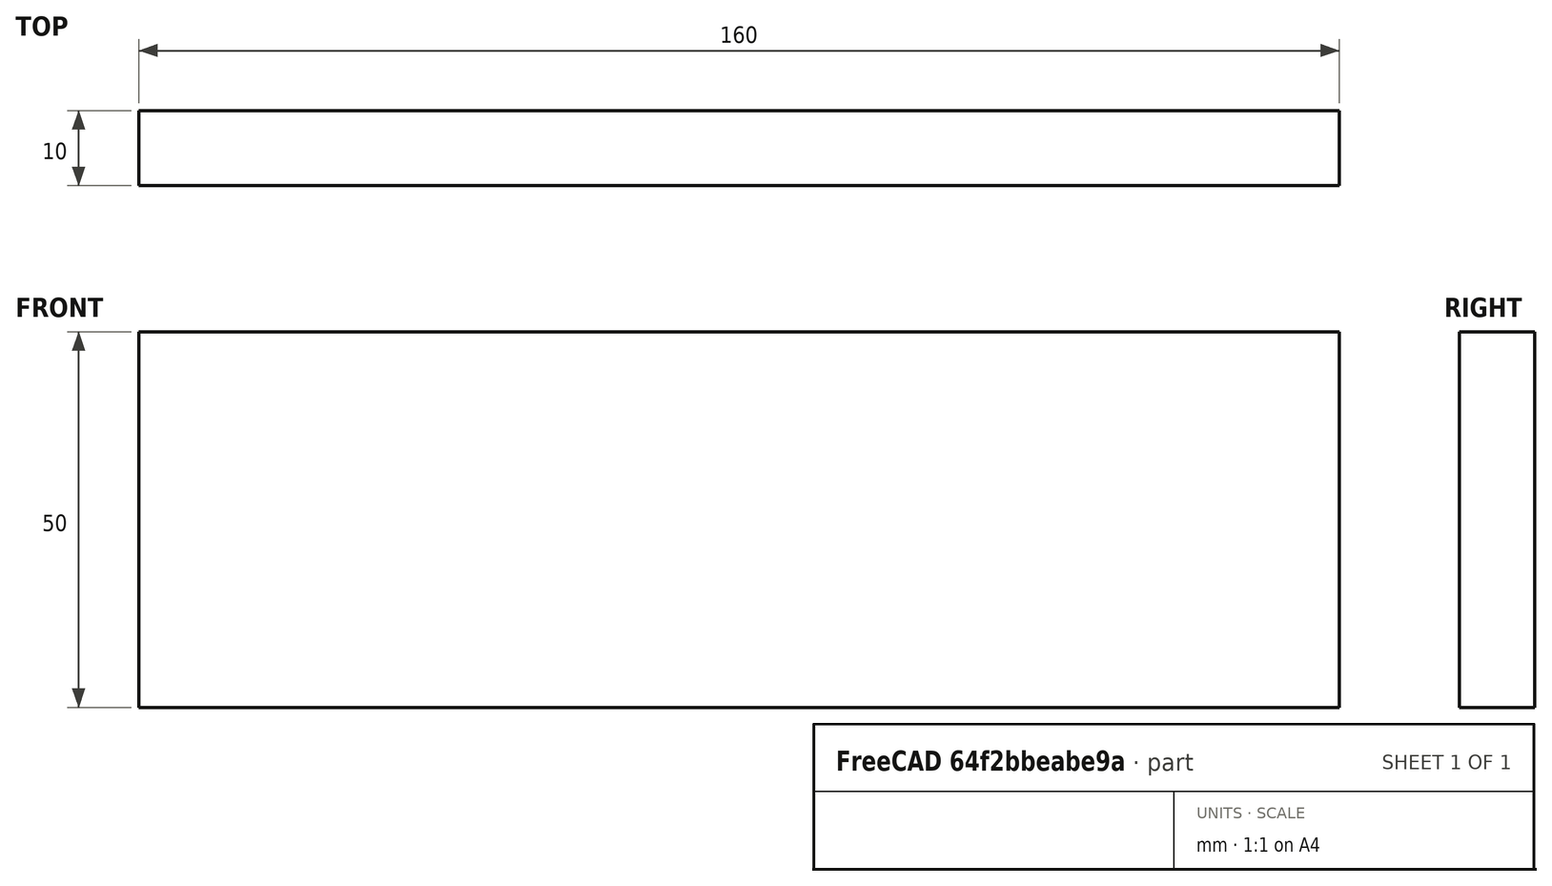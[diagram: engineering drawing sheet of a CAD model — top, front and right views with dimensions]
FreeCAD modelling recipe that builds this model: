
FCSTD DOCUMENT  (FreeCAD 0.15R4671 (Git))
Label: Flat Bar 160x10 EN10058 S235JR
License: All rights reserved
LicenseURL: http://en.wikipedia.org/wiki/All_rights_reserved
objects: Sketcher::SketchObject×1, Part::Extrusion×1
note: 2 computed .brp shape members not serialized (recipe doc carries the construction recipe); baked Part::Feature solids carry a one-line shape summary decoded from their .brp

FEATURE [Sketcher::SketchObject] Sketch
  sketch-geometry (4):
    g0: LineSegment StartX=-80 StartY=-5 StartZ=0 EndX=80 EndY=-5 EndZ=0
    g1: LineSegment StartX=80 StartY=-5 StartZ=0 EndX=80 EndY=5 EndZ=0
    g2: LineSegment StartX=80 StartY=5 StartZ=0 EndX=-80 EndY=5 EndZ=0
    g3: LineSegment StartX=-80 StartY=5 StartZ=0 EndX=-80 EndY=-5 EndZ=0
  constraints (12):
    c: Coincident(g0,g1)
    c: Coincident(g1,g2)
    c: Coincident(g2,g3)
    c: Coincident(g3,g0)
    c: Horizontal(g0)
    c: Horizontal(g2)
    c: Vertical(g1)
    c: Vertical(g3)
    c: Symmetric(g1,g2,g-2)
    c: Symmetric(g0,g1,g-1)
    c: DistanceY(g1) = 10
    c: DistanceX(g0) = 160
FEATURE [Part::Extrusion] Extrude  label="Flat Bar 160x10 EN10058 S235JR"
  Base = -> Sketch
  Dir = (0,0,50)
  Solid = true
